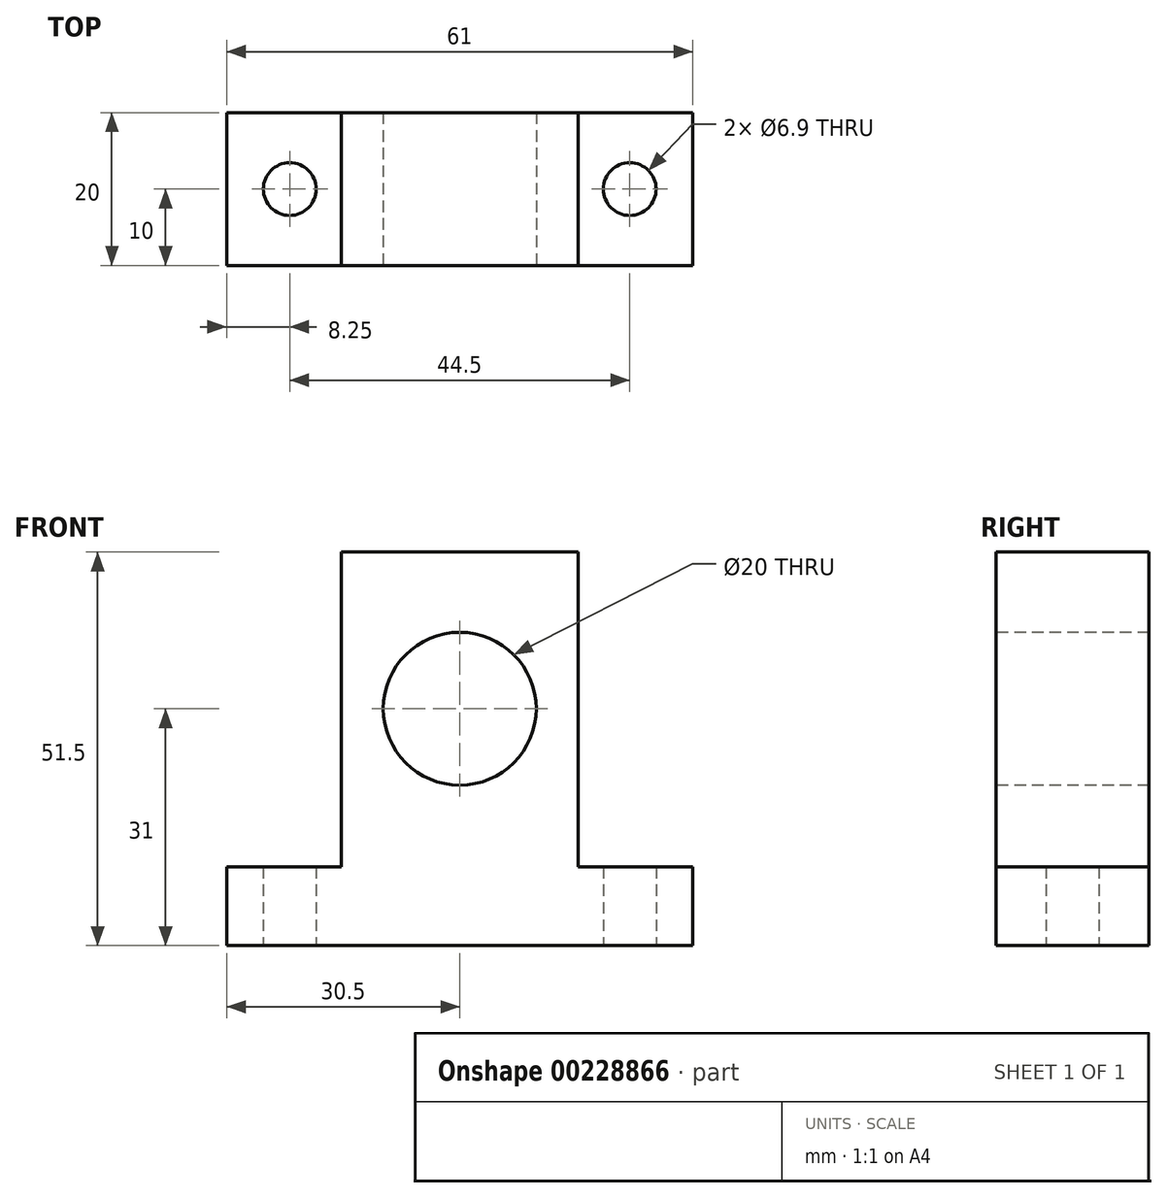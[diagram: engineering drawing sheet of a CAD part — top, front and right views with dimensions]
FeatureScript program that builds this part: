
annotation { "Feature Type Name" : "Feature", "Feature Type Description" : "" }
export const myFeature = defineFeature(function(context is Context, id is Id, definition is map)
    precondition{}
    {
        {
            var Q0;
            Q0=qCreatedBy(makeId("Front.planeOp"),FACE);
            var sketch = newSketch(context, id + "F0", { "sketchPlane" : qUnion([Q0])});
            skLineSegment(sketch, "E0.top", {"start": v(-15.5, 51.5) * mm, "end": v(15.5, 51.5) * mm});
            skLineSegment(sketch, "E0.left", {"start": v(-15.5, 10.3) * mm, "end": v(-15.5, 51.5) * mm});
            skLineSegment(sketch, "E0.right", {"start": v(15.5, 10.3) * mm, "end": v(15.5, 51.5) * mm});
            skLineSegment(sketch, "E1", {"start": v(-30.5, 0) * mm, "end": v(30.5, 0) * mm});
            skLineSegment(sketch, "E2", {"start": v(-30.5, 0) * mm, "end": v(-30.5, 10.3) * mm});
            skLineSegment(sketch, "E3", {"start": v(-30.5, 10.3) * mm, "end": v(-15.5, 10.3) * mm});
            skLineSegment(sketch, "E4", {"start": v(30.5, 0) * mm, "end": v(30.5, 10.3) * mm});
            skLineSegment(sketch, "E5", {"start": v(30.5, 10.3) * mm, "end": v(15.5, 10.3) * mm});
            skLineSegment(sketch, "E6", {"start": v(15.5, 10.3) * mm, "end": v(-15.5, 10.3) * mm, "construction": true});
            skLineSegment(sketch, "E7", {"start": v(0, 0) * mm, "end": v(0, 51.5) * mm, "construction": true});
            skSolve(sketch);
        }
        {
            var Q0;
            Q0 = qSketchRegion(id + "F0", true);
            extrude(context, id + "F1", {"entities" : qUnion([Q0]), "depth" : 20 * mm, "symmetric" : true});
        }
        {
            var Q0;
            Q0=qCreatedBy(makeId("Front.planeOp"),FACE);
            var sketch = newSketch(context, id + "F2", { "sketchPlane" : qUnion([Q0])});
            skCircle(sketch, "E8", {"center": v(0, 31) * mm, "radius": 10 * mm});
            skSolve(sketch);
        }
        {
            var Q0;
            Q0 = qSketchRegion(id + "F2", true);
            extrude(context, id + "F3", {"entities" : qUnion([Q0]), "operationType" : NewBodyOperationType.REMOVE, "oppositeDirection" : true, "depth" : 20 * mm, "symmetric" : true});
        }
        {
            var Q0;
            Q0=qCreatedBy(makeId("Top.planeOp"),FACE);
            var sketch = newSketch(context, id + "F4", { "sketchPlane" : qUnion([Q0])});
            skCircle(sketch, "E9", {"center": v(-22.25, 0) * mm, "radius": 3.45 * mm});
            skCircle(sketch, "E10", {"center": v(22.25, 0) * mm, "radius": 3.45 * mm});
            skSolve(sketch);
        }
        {
            var Q0;
            Q0 = qSketchRegion(id + "F4", true);
            extrude(context, id + "F5", {"entities" : qUnion([Q0]), "operationType" : NewBodyOperationType.REMOVE, "endBound" : BoundingType.UP_TO_NEXT, "depth" : 25 * mm});
        }
    });
